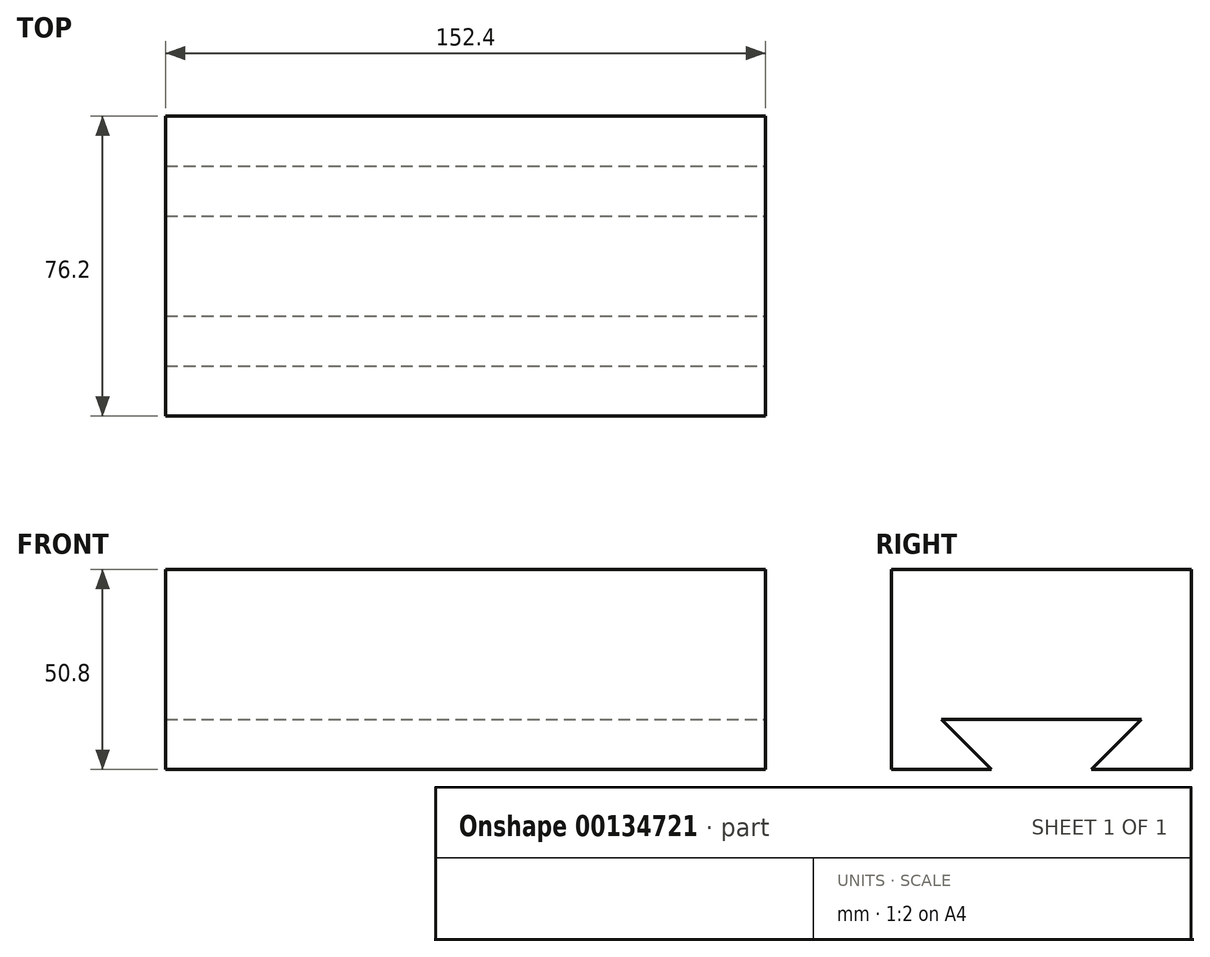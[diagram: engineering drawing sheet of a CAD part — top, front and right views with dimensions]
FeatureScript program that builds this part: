
annotation { "Feature Type Name" : "Feature", "Feature Type Description" : "" }
export const myFeature = defineFeature(function(context is Context, id is Id, definition is map)
    precondition{}
    {
        {
            var Q0;
            Q0=qCreatedBy(makeId("Top.planeOp"),FACE);
            var sketch = newSketch(context, id + "F0", { "sketchPlane" : qUnion([Q0])});
            skLineSegment(sketch, "E0.bottom", {"start": v(-76.2, 38.1) * mm, "end": v(76.2, 38.1) * mm});
            skLineSegment(sketch, "E0.top", {"start": v(-76.2, -38.1) * mm, "end": v(76.2, -38.1) * mm});
            skLineSegment(sketch, "E0.left", {"start": v(-76.2, 38.1) * mm, "end": v(-76.2, -38.1) * mm});
            skLineSegment(sketch, "E0.right", {"start": v(76.2, 38.1) * mm, "end": v(76.2, -38.1) * mm});
            skPoint(sketch, "E0.middle", {"position": v(0, 0) * mm});
            skSolve(sketch);
        }
        {
            var Q0;
            Q0 = qSketchRegion(id + "F0", true);
            extrude(context, id + "F1", {"entities" : qUnion([Q0]), "depth" : 50.8 * mm});
        }
        {
            var Q0;
            Q0=makeQuery(id+"F1.opExtrude","SWEPT_FACE",FACE,{"disambiguationData":[OSD([sQuery(id+"F0.wireOp",EDGE,"E0.right")])]});
            var sketch = newSketch(context, id + "F2", { "sketchPlane" : qUnion([Q0])});
            skLineSegment(sketch, "E1", {"start": v(-38.1, 0) * mm, "end": v(-12.7, 0) * mm});
            skLineSegment(sketch, "E2", {"start": v(-38.1, 0) * mm, "end": v(-38.1, 12.7) * mm});
            skLineSegment(sketch, "E3", {"start": v(-38.1, 12.7) * mm, "end": v(-25.4, 12.7) * mm});
            skLineSegment(sketch, "E4", {"start": v(-25.4, 12.7) * mm, "end": v(-12.7, 0) * mm});
            skLineSegment(sketch, "E5", {"start": v(-25.4, 12.7) * mm, "end": v(25.4, 12.7) * mm});
            skLineSegment(sketch, "E6", {"start": v(38.1, 0) * mm, "end": v(12.7, 0) * mm});
            skLineSegment(sketch, "E7", {"start": v(12.7, 0) * mm, "end": v(25.4, 12.7) * mm});
            skSolve(sketch);
        }
        {
            var Q0;
            {var subQ0=sQuery(id+"F2.wireOp",EDGE,"E4");Q0=makeQuery(id+"F2.imprint","IMPRINT",FACE,{"disambiguationData":[TD([[makeQuery(id+"F2.imprint","IMPRINT",EDGE,{"derivedFrom":subQ0}),1.0]])]});}
            extrude(context, id + "F3", {"entities" : qUnion([Q0]), "operationType" : NewBodyOperationType.REMOVE, "endBound" : BoundingType.THROUGH_ALL, "oppositeDirection" : true, "depth" : 25.4 * mm});
        }
    });
